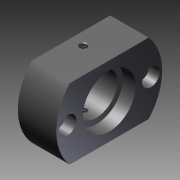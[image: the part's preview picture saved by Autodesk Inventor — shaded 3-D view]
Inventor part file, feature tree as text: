
AUTODESK INVENTOR PART (.ipt)
format: ipt  version: 2011 SP1 (Build 150282100, 282)  size: 153,600 bytes
history: native  units: mm
features: other x21, sketch x5, revolve x4, thread x3, extrude x1, pattern_linear x1
ambient origin geometry x8: Origin, YZ Plane, XZ Plane, XY Plane, X Axis, Y Axis, Z Axis, Center Point
bodies: Solid1 (feature_tree)
feature tree (35):
  revolve  "Revolution1"  [1 undecoded]
  extrude  "Extrusion1"  Depth=16.147mm TaperAngle=0.0deg
  revolve  "Revolution2"  Angle=360.0deg
  thread  "Thread1"  [1 undecoded]
  pattern_linear  "Rectangular Pattern1"  Spacing1=0.0mm  [1 undecoded]
  revolve  "Revolution3"  [1 undecoded]
  thread  "Thread2"  [1 undecoded]
  revolve  "Revolution4"  [1 undecoded]
  thread  "Thread3"  [1 undecoded]
  other  "to_bearings_XY"
  other  "to_bearings_YZ"
  other  "to_bearings_ZX"
  other  "to_bearings_X"
  other  "to_bearings_Y"
  other  "to_bearings_Z"
  other  "to_bearings_Center"
  other  "to_screw1_XY"
  other  "to_screw1_YZ"
  other  "to_screw1_ZX"
  other  "to_screw1_X"
  other  "to_screw1_Y"
  other  "to_screw1_Z"
  other  "to_screw1_Center"
  other  "to_screw2_XY"
  other  "to_screw2_YZ"
  other  "to_screw2_ZX"
  other  "to_screw2_X"
  other  "to_screw2_Y"
  other  "to_screw2_Z"
  other  "to_screw2_Center"
  sketch  "Sketch_1"  dims[d0=360.0deg d1=26.0mm d2=0.0mm]
  sketch  "Sketch_2"  dims[d3=360.0deg d4=16.147mm d5=0.0mm]
  sketch  "Sketch_3"  dims[d6=20.0mm d8=52.0mm d9=10.0mm d11=0.0mm d12=360.0deg d13=8.484mm d14=0.0mm]
  sketch  "Sketch_4"  dims[d15=360.0deg]
  sketch  "Sketch_6"  dims[d16=8.484mm d17=0.0mm d18=0.0mm]
note: 7 required parameter values undecoded (feature->parameter linkage not recoverable at this tier; creation-order binding heuristic only, values carry confidence <= 0.55)